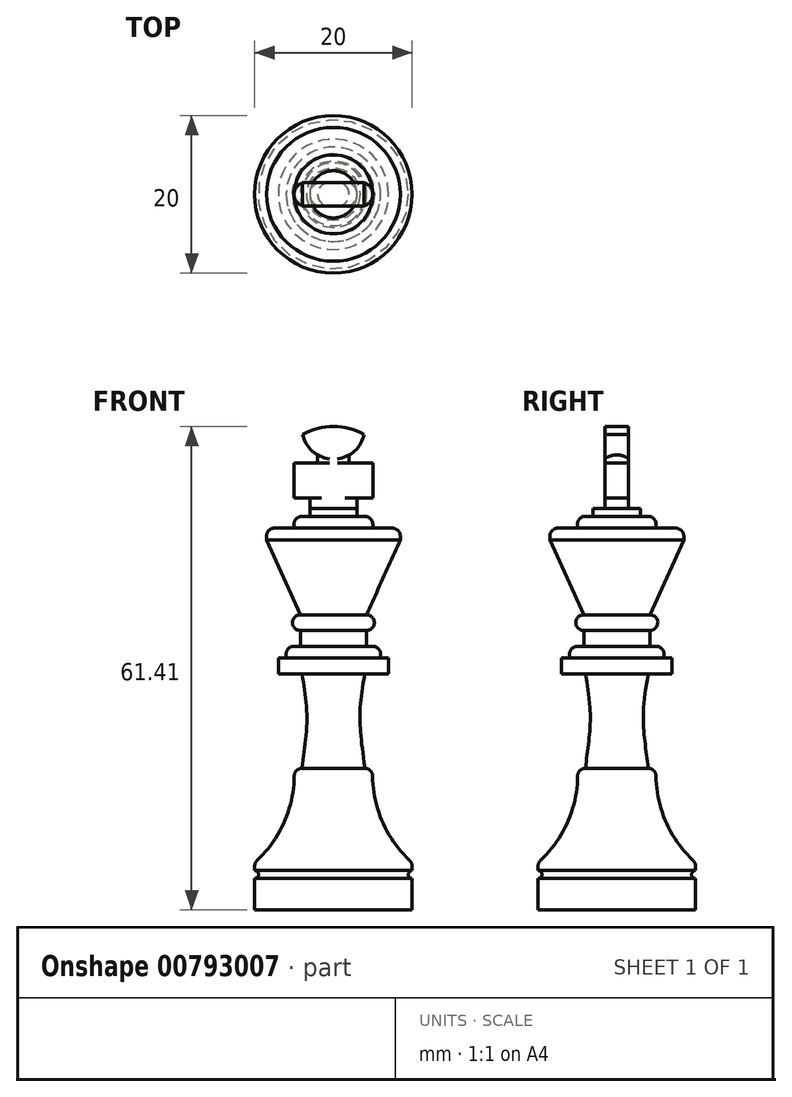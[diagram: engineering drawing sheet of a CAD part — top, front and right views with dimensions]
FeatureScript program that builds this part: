
annotation { "Feature Type Name" : "Feature", "Feature Type Description" : "" }
export const myFeature = defineFeature(function(context is Context, id is Id, definition is map)
    precondition{}
    {
        {
            var Q0;
            Q0=qCreatedBy(makeId("Front.planeOp"),FACE);
            var sketch = newSketch(context, id + "F0", { "sketchPlane" : qUnion([Q0])});
            skLineSegment(sketch, "E0.top", {"start": v(-10, 0) * mm, "end": v(10, 0) * mm, "construction": true});
            skLineSegment(sketch, "E0.left", {"start": v(10, 57) * mm, "end": v(10, 0) * mm, "construction": true});
            skLineSegment(sketch, "E0.right", {"start": v(-10, 57) * mm, "end": v(-10, 0) * mm, "construction": true});
            skLineSegment(sketch, "E1", {"start": v(0, 0) * mm, "end": v(0, 4) * mm, "construction": true});
            skLineSegment(sketch, "E2", {"start": v(0, 4) * mm, "end": v(-10, 4) * mm, "construction": true});
            skLineSegment(sketch, "E3", {"start": v(0, 4) * mm, "end": v(0, 5) * mm, "construction": true});
            skLineSegment(sketch, "E4", {"start": v(0, 5) * mm, "end": v(-10, 5) * mm, "construction": true});
            skLineSegment(sketch, "E5", {"start": v(0, 5) * mm, "end": v(0, 6) * mm, "construction": true});
            skLineSegment(sketch, "E6", {"start": v(0, 6) * mm, "end": v(-10, 6) * mm, "construction": true});
            skLineSegment(sketch, "E7", {"start": v(-9, 5) * mm, "end": v(-9, 4) * mm, "construction": true});
            skLineSegment(sketch, "E8", {"start": v(0, 6) * mm, "end": v(0, 18) * mm, "construction": true});
            skLineSegment(sketch, "E9", {"start": v(0, 18) * mm, "end": v(0, 30) * mm, "construction": true});
            skLineSegment(sketch, "E10", {"start": v(0, 0) * mm, "end": v(-10, 0) * mm});
            skLineSegment(sketch, "E11", {"start": v(-10, 4) * mm, "end": v(-10, 0) * mm});
            skArc(sketch, "E12", {"start": v(-10, 4) * mm, "mid": v(-9.5, 4.5) * mm, "end": v(-10, 5) * mm});
            skLineSegment(sketch, "E13", {"start": v(-10, 5) * mm, "end": v(-10, 6) * mm});
            skLineSegment(sketch, "E14", {"start": v(0, 18) * mm, "end": v(-10, 18) * mm, "construction": true});
            skLineSegment(sketch, "E15", {"start": v(0, 30) * mm, "end": v(-10, 30) * mm, "construction": true});
            skArc(sketch, "E16", {"start": v(-10, 6) * mm, "mid": v(-6.13, 11.43) * mm, "end": v(-5, 18) * mm});
            skLineSegment(sketch, "E17", {"start": v(-5, 18) * mm, "end": v(-4, 18) * mm});
            skLineSegment(sketch, "E18", {"start": v(0.27, 32) * mm, "end": v(-10, 32) * mm, "construction": true});
            skFitSpline(sketch, "E19", {"points": [v(-4, 18) * mm, v(-4, 30) * mm], "startDerivative": vector(2.23, 16.47) * mm, "endDerivative": vector(-2.8, 14.94) * mm});
            skLineSegment(sketch, "E20", {"start": v(-4, 30) * mm, "end": v(-7, 30) * mm});
            skLineSegment(sketch, "E21", {"start": v(-7, 30) * mm, "end": v(-7, 32) * mm});
            skLineSegment(sketch, "E22", {"start": v(-7, 32) * mm, "end": v(-6, 32) * mm});
            skLineSegment(sketch, "E23", {"start": v(0, 33.5) * mm, "end": v(-10, 33.5) * mm, "construction": true});
            skLineSegment(sketch, "E24", {"start": v(0, 35.5) * mm, "end": v(-10, 35.5) * mm, "construction": true});
            skLineSegment(sketch, "E25", {"start": v(0, 37.5) * mm, "end": v(-10, 37.5) * mm, "construction": true});
            skLineSegment(sketch, "E26", {"start": v(-6, 32) * mm, "end": v(-6, 33.5) * mm});
            skLineSegment(sketch, "E27", {"start": v(-6, 33.5) * mm, "end": v(-4.2, 33.5) * mm});
            skLineSegment(sketch, "E28", {"start": v(-4.2, 33.5) * mm, "end": v(-4.2, 35.5) * mm});
            skArc(sketch, "E29", {"start": v(-4.2, 37.5) * mm, "mid": v(-5.2, 36.5) * mm, "end": v(-4.2, 35.5) * mm});
            skLineSegment(sketch, "E30", {"start": v(-10, 47) * mm, "end": v(0, 47) * mm, "construction": true});
            skLineSegment(sketch, "E31", {"start": v(-10, 48.5) * mm, "end": v(0, 48.5) * mm, "construction": true});
            skLineSegment(sketch, "E32", {"start": v(-8.5, 48.5) * mm, "end": v(-8.5, 47) * mm});
            skLineSegment(sketch, "E33", {"start": v(0, 50) * mm, "end": v(-10, 50) * mm, "construction": true});
            skLineSegment(sketch, "E34", {"start": v(-10, 51) * mm, "end": v(0, 51) * mm, "construction": true});
            skLineSegment(sketch, "E35", {"start": v(-3, 50) * mm, "end": v(-3, 51) * mm});
            skLineSegment(sketch, "E36", {"start": v(-10, 52) * mm, "end": v(0, 52) * mm, "construction": true});
            skLineSegment(sketch, "E37", {"start": v(-8.5, 47) * mm, "end": v(-4.2, 37.5) * mm});
            skLineSegment(sketch, "E38", {"start": v(-8.5, 48.5) * mm, "end": v(-5, 48.5) * mm});
            skLineSegment(sketch, "E39", {"start": v(-5, 48.5) * mm, "end": v(-5, 50) * mm});
            skLineSegment(sketch, "E40", {"start": v(-5, 50) * mm, "end": v(-3, 50) * mm});
            skLineSegment(sketch, "E41", {"start": v(-3, 51) * mm, "end": v(0, 51) * mm});
            skLineSegment(sketch, "E42", {"start": v(0, 51) * mm, "end": v(0, 0) * mm});
            skSolve(sketch);
        }
        {
            var Q0;
            Q0=qSketchRegion(id+"F0",true);
            var Q1;
            Q1=sQuery(id+"F0.wireOp",EDGE,"E42");
            revolve(context, id + "F1", {"surfaceOperationType" : NewSurfaceOperationType.NEW, "entities" : qUnion([Q0]), "axis" : qUnion([Q1]), "revolveType" : RevolveType.FULL});
        }
        {
            var Q0;
            Q0=makeQuery(id+"F1.opRevolve","SWEPT_EDGE",EDGE,{"disambiguationData":[OSD([sQuery(id+"F0.wireOp",EDGE,"E13"),sQuery(id+"F0.wireOp",EDGE,"E16")])]});
            var Q1;
            Q1=makeQuery(id+"F1.opRevolve","SWEPT_EDGE",EDGE,{"disambiguationData":[OSD([sQuery(id+"F0.wireOp",EDGE,"E16"),sQuery(id+"F0.wireOp",EDGE,"E17")])]});
            var Q2;
            Q2=makeQuery(id+"F1.opRevolve","SWEPT_EDGE",EDGE,{"disambiguationData":[OSD([sQuery(id+"F0.wireOp",EDGE,"E26"),sQuery(id+"F0.wireOp",EDGE,"E27")])]});
            var Q3;
            Q3=makeQuery(id+"F1.opRevolve","SWEPT_EDGE",EDGE,{"disambiguationData":[OSD([sQuery(id+"F0.wireOp",EDGE,"E32"),sQuery(id+"F0.wireOp",EDGE,"E38")])]});
            var Q4;
            Q4=makeQuery(id+"F1.opRevolve","SWEPT_EDGE",EDGE,{"disambiguationData":[OSD([sQuery(id+"F0.wireOp",EDGE,"E39"),sQuery(id+"F0.wireOp",EDGE,"E40")])]});
            fillet(context, id + "F2", {"entities" : qUnion([Q0, Q1, Q2, Q3, Q4]), "radius" : 1 * mm, "tangentPropagation" : true, "allowEdgeOverflow" : false});
        }
        {
            var Q0;
            Q0=qCreatedBy(makeId("Front.planeOp"),FACE);
            var sketch = newSketch(context, id + "F3", { "sketchPlane" : qUnion([Q0])});
            skLineSegment(sketch, "E43", {"start": v(0, 51) * mm, "end": v(-3, 51) * mm});
            skLineSegment(sketch, "E44", {"start": v(-3, 51) * mm, "end": v(-3, 52.3) * mm});
            skLineSegment(sketch, "E45", {"start": v(-3, 52.3) * mm, "end": v(-5, 52.3) * mm});
            skLineSegment(sketch, "E46", {"start": v(-5, 52.3) * mm, "end": v(-5, 56.8) * mm});
            skLineSegment(sketch, "E47", {"start": v(5, 56.8) * mm, "end": v(5, 52.3) * mm});
            skLineSegment(sketch, "E48", {"start": v(5, 52.3) * mm, "end": v(3, 52.3) * mm});
            skLineSegment(sketch, "E49", {"start": v(3, 52.3) * mm, "end": v(3, 51) * mm});
            skLineSegment(sketch, "E50", {"start": v(3, 51) * mm, "end": v(0, 51) * mm});
            skLineSegment(sketch, "E51", {"start": v(-5, 56.8) * mm, "end": v(-2, 56.8) * mm});
            skLineSegment(sketch, "E52", {"start": v(-2, 56.8) * mm, "end": v(-2, 57.8) * mm});
            skArc(sketch, "E53", {"start": v(-3.9, 60.4) * mm, "mid": v(-3.22, 58.9) * mm, "end": v(-2, 57.8) * mm});
            skLineSegment(sketch, "E54", {"start": v(5, 56.8) * mm, "end": v(2, 56.8) * mm});
            skLineSegment(sketch, "E55", {"start": v(2, 56.8) * mm, "end": v(2, 57.8) * mm});
            skLineSegment(sketch, "E56", {"start": v(0, 51) * mm, "end": v(0, 61.4) * mm, "construction": true});
            skArc(sketch, "E57", {"start": v(2, 57.8) * mm, "mid": v(3.22, 58.9) * mm, "end": v(3.9, 60.4) * mm});
            skArc(sketch, "E58", {"start": v(3.9, 60.4) * mm, "mid": v(0, 61.4) * mm, "end": v(-3.9, 60.4) * mm});
            skSolve(sketch);
        }
        {
            var Q0;
            Q0 = qSketchRegion(id + "F3", true);
            extrude(context, id + "F4", {"entities" : qUnion([Q0]), "operationType" : NewBodyOperationType.ADD, "endBound" : BoundingType.SYMMETRIC, "depth" : 3 * mm, "offsetDistance" : 25 * mm});
        }
        {
            var Q0;
            Q0=makeQuery(id+"F4.opExtrude","CAP_EDGE",EDGE,{"disambiguationData":[OSD([sQuery(id+"F3.wireOp",EDGE,"E46")])],"isStart":false});
            var Q1;
            Q1=makeQuery(id+"F4.opExtrude","CAP_EDGE",EDGE,{"disambiguationData":[OSD([sQuery(id+"F3.wireOp",EDGE,"E46")])],"isStart":true});
            var Q2;
            Q2=makeQuery(id+"F4.opExtrude","CAP_EDGE",EDGE,{"disambiguationData":[OSD([sQuery(id+"F3.wireOp",EDGE,"E47")])],"isStart":false});
            var Q3;
            Q3=makeQuery(id+"F4.opExtrude","CAP_EDGE",EDGE,{"disambiguationData":[OSD([sQuery(id+"F3.wireOp",EDGE,"E47")])],"isStart":true});
            var Q4;
            Q4=makeQuery(id+"F4.opExtrude","CAP_EDGE",EDGE,{"disambiguationData":[OSD([sQuery(id+"F3.wireOp",EDGE,"E52")])],"isStart":false});
            var Q5;
            Q5=makeQuery(id+"F4.opExtrude","CAP_EDGE",EDGE,{"disambiguationData":[OSD([sQuery(id+"F3.wireOp",EDGE,"E55")])],"isStart":false});
            var Q6;
            Q6=makeQuery(id+"F4.opExtrude","CAP_EDGE",EDGE,{"disambiguationData":[OSD([sQuery(id+"F3.wireOp",EDGE,"E52")])],"isStart":true});
            var Q7;
            Q7=makeQuery(id+"F4.opExtrude","CAP_EDGE",EDGE,{"disambiguationData":[OSD([sQuery(id+"F3.wireOp",EDGE,"E55")])],"isStart":true});
            var Q8;
            Q8=makeQuery(id+"F4.opExtrude","CAP_EDGE",EDGE,{"disambiguationData":[OSD([sQuery(id+"F3.wireOp",EDGE,"E49")])],"isStart":true});
            var Q9;
            Q9=makeQuery(id+"F4.opExtrude","CAP_EDGE",EDGE,{"disambiguationData":[OSD([sQuery(id+"F3.wireOp",EDGE,"E49")])],"isStart":false});
            var Q10;
            Q10=makeQuery(id+"F4.opExtrude","CAP_EDGE",EDGE,{"disambiguationData":[OSD([sQuery(id+"F3.wireOp",EDGE,"E44")])],"isStart":false});
            var Q11;
            Q11=makeQuery(id+"F4.opExtrude","CAP_EDGE",EDGE,{"disambiguationData":[OSD([sQuery(id+"F3.wireOp",EDGE,"E44")])],"isStart":true});
            fillet(context, id + "F5", {"entities" : qUnion([Q0, Q1, Q2, Q3, Q4, Q5, Q6, Q7, Q8, Q9, Q10, Q11]), "radius" : 1.5 * mm, "tangentPropagation" : true, "allowEdgeOverflow" : false});
        }
    });
